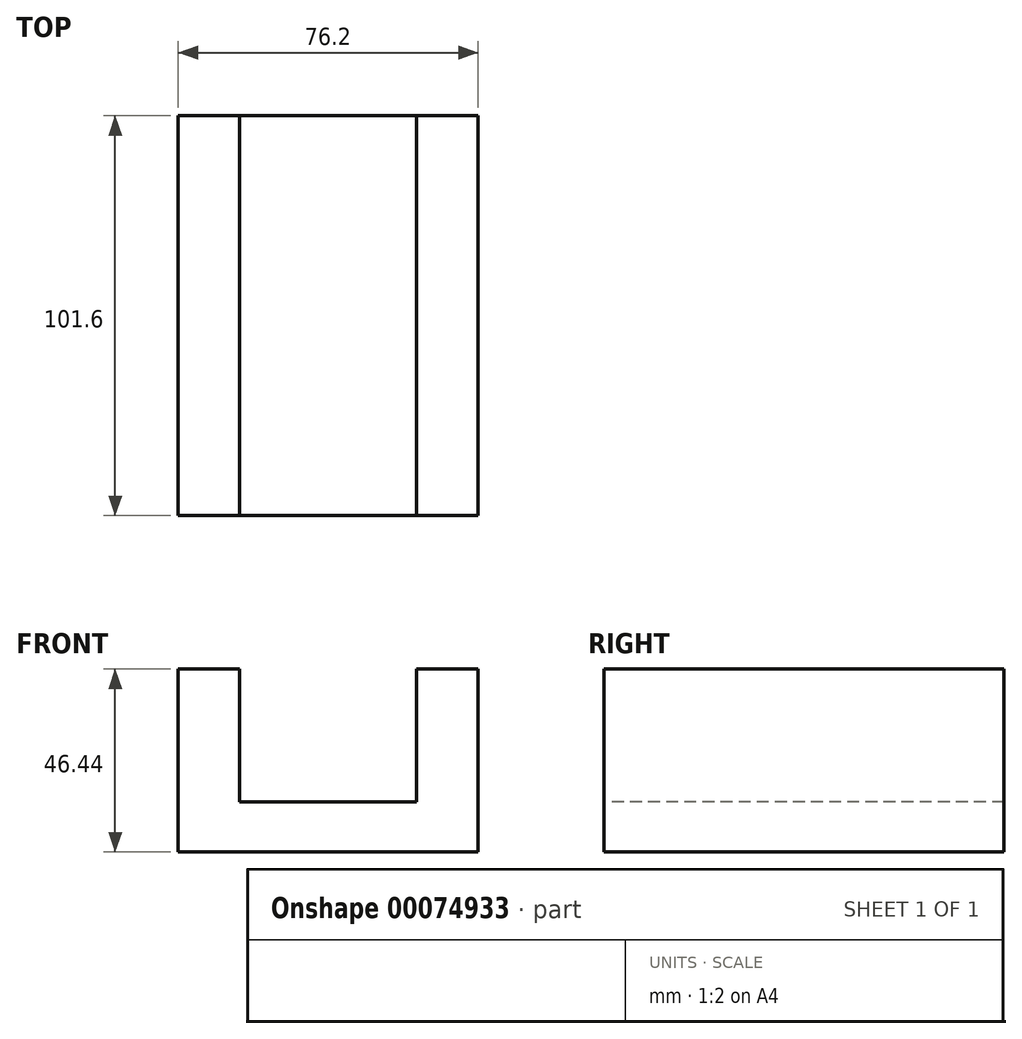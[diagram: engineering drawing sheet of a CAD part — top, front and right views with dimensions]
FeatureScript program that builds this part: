
annotation { "Feature Type Name" : "Feature", "Feature Type Description" : "" }
export const myFeature = defineFeature(function(context is Context, id is Id, definition is map)
    precondition{}
    {
        {
            var Q0;
            Q0=qCreatedBy(makeId("Top.planeOp"),FACE);
            var sketch = newSketch(context, id + "F0", { "sketchPlane" : qUnion([Q0])});
            skLineSegment(sketch, "E0", {"start": v(0, 50.8) * mm, "end": v(38.1, 50.8) * mm});
            skLineSegment(sketch, "E1", {"start": v(38.1, 50.8) * mm, "end": v(38.1, 0) * mm});
            skLineSegment(sketch, "E2.MirrorCS", {"start": v(0, -50.8) * mm, "end": v(38.1, -50.8) * mm});
            skLineSegment(sketch, "E3.MirrorCS", {"start": v(38.1, -50.8) * mm, "end": v(38.1, 0) * mm});
            skLineSegment(sketch, "E4.MirrorCS", {"start": v(0, 50.8) * mm, "end": v(-38.1, 50.8) * mm});
            skLineSegment(sketch, "E5.MirrorCS", {"start": v(-38.1, 50.8) * mm, "end": v(-38.1, 0) * mm});
            skLineSegment(sketch, "E6.MirrorCS", {"start": v(-38.1, -50.8) * mm, "end": v(-38.1, 0) * mm});
            skLineSegment(sketch, "E7.MirrorCS", {"start": v(0, -50.8) * mm, "end": v(-38.1, -50.8) * mm});
            skSolve(sketch);
        }
        {
            var Q0;
            Q0 = qSketchRegion(id + "F0", true);
            extrude(context, id + "F1", {"entities" : qUnion([Q0]), "endBound" : BoundingType.SYMMETRIC, "depth" : 12.7 * mm});
        }
        {
            var Q0;
            Q0=makeQuery(id+"F1.opExtrude","SWEPT_FACE",FACE,{"disambiguationData":[OSD([sQuery(id+"F0.wireOp",EDGE,"E2.MirrorCS"),sQuery(id+"F0.wireOp",EDGE,"E7.MirrorCS")])]});
            var sketch = newSketch(context, id + "F2", { "sketchPlane" : qUnion([Q0])});
            skLineSegment(sketch, "E8", {"start": v(-38.1, 6.35) * mm, "end": v(-38.1, 40.1) * mm});
            skLineSegment(sketch, "E9", {"start": v(-38.1, 40.1) * mm, "end": v(-22.46, 40.1) * mm});
            skLineSegment(sketch, "E10", {"start": v(-22.46, 40.1) * mm, "end": v(-22.46, 6.35) * mm});
            skLineSegment(sketch, "E11", {"start": v(-22.46, 6.35) * mm, "end": v(-38.1, 6.35) * mm});
            skSolve(sketch);
        }
        {
            var Q0;
            Q0 = qSketchRegion(id + "F2", true);
            extrude(context, id + "F3", {"entities" : qUnion([Q0]), "oppositeDirection" : true, "depth" : 101.6 * mm});
        }
        {
            var Q0;
            Q0=makeQuery(id+"F3.opExtrude","SWEPT_BODY",BODY,{"disambiguationData":[OSD([sQuery(id+"F2.wireOp",EDGE,"E8"),sQuery(id+"F2.wireOp",EDGE,"E9"),sQuery(id+"F2.wireOp",EDGE,"E10"),sQuery(id+"F2.wireOp",EDGE,"E11")])]});
            var Q1;
            Q1=qCreatedBy(makeId("Right.planeOp"),FACE);
            mirror(context, id + "F4", {"operationType" : NewBodyOperationType.ADD, "entities" : qUnion([Q0]), "mirrorPlane" : qUnion([Q1])});
        }
    });
